# Revit family: Červinka_Přenosný hasicí přístroj_Práškový P6 BETA-Z
name_source: partatom
category: Speciální vybavení
units: mm (PartAtom-declared; Revit-internal decimal feet)

## family parameters
Bod výpočtu místnosti = Ne
Kóta kulaté spojky = Použít průměr
Ořezat dutým tvarem při načtení = Ne
Sdílené = Ne
Typ dílu = Normální
Vždy vertikální = Ano
Založené na pracovní rovině = Ano

## types (1)
- P6 BETA-Z
    Cena = 0 $
    Hasicí schopnost_ = 34A / 183B / C
    Hasivo = HJ ABC Universal
    Hmotnost = 9.60 kg
    Hmotnost hasiva = 6.00 kg
    Komentáře k typům = Přenosný práškový hasicí přístroj
    Kód sestavy = PZ.
    Kód_ = 0111
    Materiál hadice = Černá
    Maximální teplota použití = 60 °C
    Minimální teplota použití = -30 °C
    Model = P6 BETA-Z
    Objem lahve = 7.60 L
    Popis = Přenosný hasicí přístroj
    Povrchová úprava lahve = Červená
    Pracovní tlak = 15.0 bar
    Průměr lahve = 160 mm  [stored 0.524934 ft]
    Splnění norem = EN3
    Typ zařízení_ = P6 BETA-Z
    Třída požáru A = Ano
    Třída požáru B = Ano
    Třída požáru C = Ano
    Třída požáru D = Ne
    Třída požáru F = Ne
    URL = http://www.hasicitechnika.com
    Výchozí výška = 1500 mm  [stored 4.92126 ft]
    Výrobce = ČERVINKA - CZECH REPUBLIC s.r.o.
    Výška k ventilu = 430 mm  [stored 1.41076 ft]
    Výška_ = 525 mm
    Šířka_ = 185 mm  [stored 0.606955 ft]

note: [stored X ft] marks values corroborated as IEEE doubles in the binary element streams (Revit-internal decimal feet)
